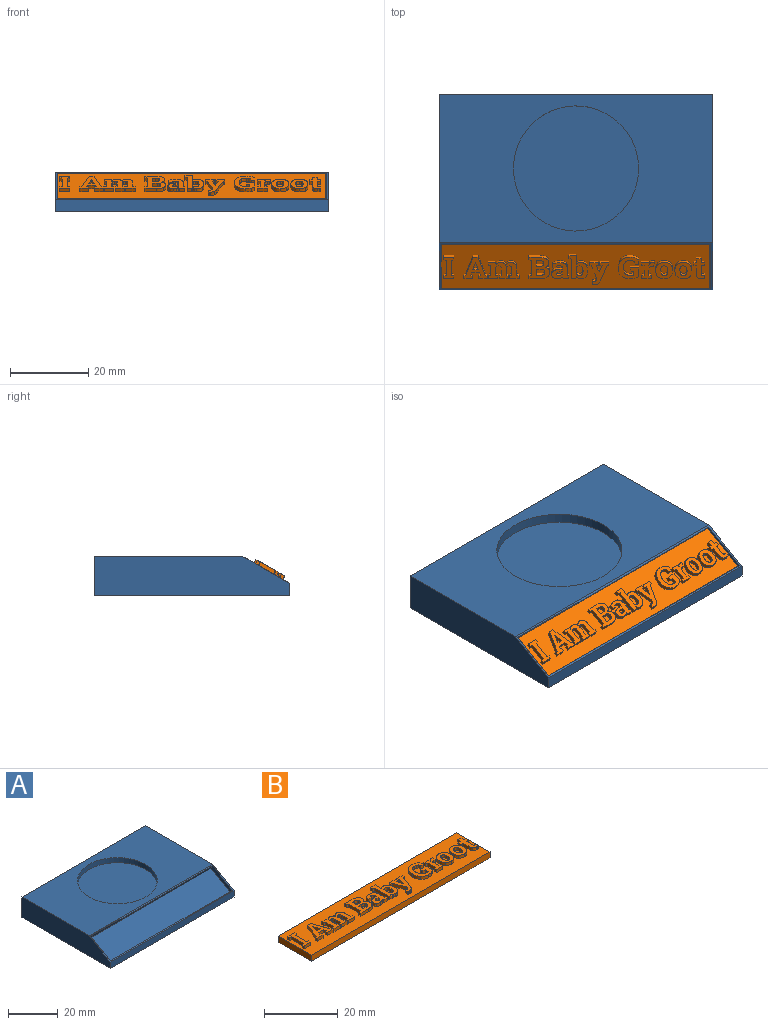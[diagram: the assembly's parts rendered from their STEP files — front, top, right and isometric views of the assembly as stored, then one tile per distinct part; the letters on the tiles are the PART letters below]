
ASSEMBLY  parts=2 mates=1
PART A: 14 faces, bbox 70x50x10 mm
  f0: plane 70x10mm, normal (0,1,0), area 700mm2, adj f1,f3,f4,f5
  f1: plane 50x10mm, normal (-1,0,0), area 458.4mm2, adj f0,f2,f4,f5,f6
  f2: plane 70x3.07mm, normal (0,-1,0), area 215mm2, adj f1,f3,f5,f6
  f3: plane 50x10mm, normal (1,0,0), area 458.4mm2, adj f0,f2,f4,f5,f6
  f4: plane 70x38mm, normal (0,0,1), area 1855.8mm2, adj f0,f1,f3,f6,f7
  f5: plane 70x50mm, normal (0,0,-1), area 3500mm2, adj f0,f1,f2,f3
  f6: plane 70x12mm, normal (0,-0.5,0.87), area 82.9mm2, adj f1,f2,f3,f4,f9,f10,f11,f12
  f7: cylinder r=16mm len=32mm, axis (0,0,1), area 251.3mm2, adj f4,f8
  f8: plane 32x32mm, normal (0,0,1), area 804.2mm2, adj f7
  f9: plane 12.13x8.16mm, normal (1,0,0), area 25.7mm2, adj f6,f10,f12,f13
  f10: plane 69x1.73mm, normal (0,0.87,0.5), area 138mm2, adj f6,f9,f11,f13
  f11: plane 12.13x8.16mm, normal (-1,0,0), area 25.7mm2, adj f6,f10,f12,f13
  f12: plane 69x1.73mm, normal (0,-0.87,-0.5), area 138mm2, adj f6,f9,f11,f13
  f13: plane 69x11.13mm, normal (0,-0.5,0.87), area 887.1mm2, adj f9,f10,f11,f12
PART B: 321 faces, bbox 68.5x12.7x3 mm
  f0: plane 68.5x12.7mm, normal (0,0,1), area 673mm2, adj f1,f2,f3,f4,f6,f7,f8,f9
  f1: plane 68.5x2mm, normal (0,1,0), area 137mm2, adj f0,f2,f4,f5
  f2: plane 12.7x2mm, normal (-1,0,0), area 25.4mm2, adj f0,f1,f3,f5
  f3: plane 68.5x2mm, normal (0,-1,0), area 137mm2, adj f0,f2,f4,f5
  f4: plane 12.7x2mm, normal (1,0,0), area 25.4mm2, adj f0,f1,f3,f5
  f5: plane 68.5x12.7mm, normal (0,0,-1), area 870mm2, adj f1,f2,f3,f4
  f6: plane 1x0.67mm, normal (-0.19,-0.98,0), area 0.7mm2, adj f0,f7,f17,f18
  f7: plane 4.46x1mm, normal (-1,0,0), area 4.5mm2, adj f0,f6,f8,f18
  f8: plane 1x0.67mm, normal (-0.19,0.98,0), area 0.7mm2, adj f0,f7,f9,f18
  f9: plane 1x0.75mm, normal (-1,0,0), area 0.7mm2, adj f0,f8,f10,f18
  f10: plane 2.57x1mm, normal (0,-1,0), area 2.6mm2, adj f0,f9,f11,f18
  f11: plane 1x0.75mm, normal (1,0,0), area 0.7mm2, adj f0,f10,f12,f18
  f12: plane 1x0.67mm, normal (0.19,0.98,0), area 0.7mm2, adj f0,f11,f13,f18
  f13: plane 4.46x1mm, normal (1,0,0), area 4.5mm2, adj f0,f12,f14,f18
  f14: plane 1x0.67mm, normal (0.19,-0.98,0), area 0.7mm2, adj f0,f13,f15,f18
  f15: plane 1x0.75mm, normal (1,0,0), area 0.8mm2, adj f0,f14,f16,f18
  f16: plane 2.57x1mm, normal (0,1,0), area 2.6mm2, adj f0,f15,f17,f18
  f17: plane 1x0.75mm, normal (-1,0,0), area 0.8mm2, adj f0,f6,f16,f18
  f18: plane 6.21x2.57mm, normal (0,0,1), area 9.9mm2, adj f6,f7,f8,f9,f10,f11,f12,f13
  f19: plane 1x0.75mm, normal (-1,0,0), area 0.7mm2, adj f0,f20,f38,f39
  f20: plane 2.12x1mm, normal (0,-1,0), area 2.1mm2, adj f0,f19,f21,f39
  f21: plane 1x0.75mm, normal (1,0,0), area 0.7mm2, adj f0,f20,f22,f39
  f22: plane 1x0.43mm, normal (0.18,0.98,0), area 0.4mm2, adj f0,f21,f23,f39
  f23: plane 1x0.85mm, normal (0.95,-0.3,0), area 0.9mm2, adj f0,f22,f24,f39
  f24: plane 2.01x1mm, normal (0,-1,0), area 2mm2, adj f0,f23,f25,f39
  f25: plane 1x0.85mm, normal (-0.95,-0.3,0), area 0.9mm2, adj f0,f24,f26,f39
  f26: plane 1x0.43mm, normal (-0.17,0.98,0), area 0.4mm2, adj f0,f25,f27,f39
  f27: plane 1x0.75mm, normal (-1,0,0), area 0.7mm2, adj f0,f26,f28,f39
  f28: plane 2.12x1mm, normal (0,-1,0), area 2.1mm2, adj f0,f27,f29,f39
  f29: plane 1x0.75mm, normal (1,0,0), area 0.7mm2, adj f0,f28,f30,f39
  f30: plane 1x0.44mm, normal (0.14,0.99,0), area 0.4mm2, adj f0,f29,f31,f39
  f31: plane 5.4x1.88mm, normal (0.94,0.33,0), area 5.7mm2, adj f0,f30,f32,f39
  f32: plane 1.28x1mm, normal (0,1,0), area 1.3mm2, adj f0,f31,f33,f39
  f33: plane 5.4x1.89mm, normal (-0.94,0.33,0), area 5.7mm2, adj f0,f32,f38,f39
  f34: plane 2.19x1mm, normal (0.95,-0.3,0), area 2.3mm2, adj f35,f37,f39,f40
  f35: plane 1x0.02mm, normal (0,-1,0), area 0mm2, adj f34,f36,f39,f40
  f36: plane 2.19x1mm, normal (-0.95,-0.3,0), area 2.3mm2, adj f35,f37,f39,f40
  f37: plane 1.43x1mm, normal (0,1,0), area 1.4mm2, adj f34,f36,f39,f40
  f38: plane 1x0.44mm, normal (-0.14,0.99,0), area 0.4mm2, adj f0,f19,f33,f39
  f39: plane 6.21x5.93mm, normal (0,0,1), area 16.9mm2, adj f19,f20,f21,f22,f23,f24,f25,f26
  f40: plane 2.19x1.43mm, normal (0,0,1), area 1.6mm2, adj f34,f35,f36,f37
  f41: plane 1x0.67mm, normal (-0.19,-0.98,0), area 0.7mm2, adj f0,f42,f83,f84
  f42: plane 2.86x1mm, normal (-1,0,0), area 2.9mm2, adj f0,f41,f43,f84
  f43: plane 1x0.6mm, normal (-0.21,0.98,0), area 0.6mm2, adj f0,f42,f44,f84
  f44: plane 1x0.75mm, normal (-1,0,0), area 0.7mm2, adj f0,f43,f45,f84
  f45: plane 2.38x1mm, normal (0,-1,0), area 2.4mm2, adj f0,f44,f46,f84
  f46: plane 1x0.75mm, normal (1,0,0), area 0.7mm2, adj f0,f45,f47,f84
  f47: plane 1x0.54mm, normal (0.23,0.97,0), area 0.6mm2, adj f0,f46,f48,f84
  f48: plane 2.49x1mm, normal (1,0,0), area 2.5mm2, adj f0,f47,f49,f84
  f49: extruded ~1x0.31mm, area 0.4mm2, adj f0,f48,f50,f84
  f50: extruded ~1x0.44mm, area 0.5mm2, adj f0,f49,f51,f84
  f51: extruded ~1x0.51mm, area 0.6mm2, adj f0,f50,f52,f84
  f52: extruded ~1x0.72mm, area 0.8mm2, adj f0,f51,f53,f84
  f53: plane 1.92x1mm, normal (-1,0,0), area 1.9mm2, adj f0,f52,f54,f84
  f54: plane 1x0.5mm, normal (-0.25,0.97,0), area 0.5mm2, adj f0,f53,f55,f84
  f55: plane 1x0.75mm, normal (-1,0,0), area 0.7mm2, adj f0,f54,f56,f84
  f56: plane 2.25x1mm, normal (0,-1,0), area 2.2mm2, adj f0,f55,f57,f84
  f57: plane 1x0.75mm, normal (1,0,0), area 0.7mm2, adj f0,f56,f58,f84
  f58: plane 1x0.5mm, normal (0.25,0.97,0), area 0.5mm2, adj f0,f57,f59,f84
  f59: plane 2.16x1mm, normal (1,0,0), area 2.2mm2, adj f0,f58,f60,f84
  f60: extruded ~1x0.12mm, area 0.1mm2, adj f0,f59,f61,f84
  f61: extruded ~1x0.14mm, area 0.1mm2, adj f0,f60,f62,f84
  f62: extruded ~1x0.33mm, area 0.5mm2, adj f0,f61,f63,f84
  f63: extruded ~1x0.46mm, area 0.5mm2, adj f0,f62,f64,f84
  f64: extruded ~1x0.51mm, area 0.6mm2, adj f0,f63,f65,f84
  f65: extruded ~1x0.73mm, area 0.8mm2, adj f0,f64,f66,f84
  f66: plane 1.92x1mm, normal (-1,0,0), area 1.9mm2, adj f0,f65,f67,f84
  f67: plane 1x0.54mm, normal (-0.23,0.97,0), area 0.6mm2, adj f0,f66,f68,f84
  f68: plane 1x0.75mm, normal (-1,0,0), area 0.7mm2, adj f0,f67,f69,f84
  f69: plane 2.39x1mm, normal (0,-1,0), area 2.4mm2, adj f0,f68,f70,f84
  f70: plane 1x0.75mm, normal (1,0,0), area 0.7mm2, adj f0,f69,f71,f84
  f71: plane 1x0.6mm, normal (0.21,0.98,0), area 0.6mm2, adj f0,f70,f72,f84
  f72: plane 1.92x1mm, normal (1,0,0), area 1.9mm2, adj f0,f71,f73,f84
  f73: extruded ~1.44x1mm, area 1.5mm2, adj f0,f72,f74,f84
  f74: extruded ~1.08x1mm, area 1.2mm2, adj f0,f73,f75,f84
  f75: extruded ~1x0.8mm, area 0.8mm2, adj f0,f74,f76,f84
  f76: extruded ~1x0.58mm, area 0.8mm2, adj f0,f75,f77,f84
  f77: extruded ~1x0.59mm, area 0.8mm2, adj f0,f76,f78,f84
  f78: extruded ~1x0.76mm, area 0.8mm2, adj f0,f77,f79,f84
  f79: extruded ~1x0.77mm, area 0.8mm2, adj f0,f78,f80,f84
  f80: extruded ~1x0.56mm, area 0.8mm2, adj f0,f79,f81,f84
  f81: plane 1x0.61mm, normal (1,0.08,0), area 0.6mm2, adj f0,f80,f82,f84
  f82: plane 1.82x1mm, normal (0,1,0), area 1.8mm2, adj f0,f81,f83,f84
  f83: plane 1x0.75mm, normal (-1,0,0), area 0.8mm2, adj f0,f41,f82,f84
  f84: plane 7.87x4.7mm, normal (0,0,1), area 22.5mm2, adj f41,f42,f43,f44,f45,f46,f47,f48
  f85: plane 2.76x1mm, normal (0,1,0), area 2.8mm2, adj f0,f86,f113,f114
  f86: plane 1x0.75mm, normal (-1,0,0), area 0.8mm2, adj f0,f85,f87,f114
  f87: plane 1x0.66mm, normal (-0.19,-0.98,0), area 0.7mm2, adj f0,f86,f88,f114
  f88: plane 4.46x1mm, normal (-1,0,0), area 4.5mm2, adj f0,f87,f89,f114
  f89: plane 1x0.66mm, normal (-0.19,0.98,0), area 0.7mm2, adj f0,f88,f90,f114
  f90: plane 1x0.75mm, normal (-1,0,0), area 0.7mm2, adj f0,f89,f91,f114
  f91: plane 3.06x1mm, normal (0,-1,0), area 3.1mm2, adj f0,f90,f92,f114
  f92: extruded ~1.67x1mm, area 1.8mm2, adj f0,f91,f93,f114
  f93: extruded ~1.35x1mm, area 1.5mm2, adj f0,f92,f94,f114
  f94: extruded ~1x0.91mm, area 1mm2, adj f0,f93,f95,f114
  f95: extruded ~1x0.84mm, area 1mm2, adj f0,f94,f96,f114
  f96: extruded ~1x0.66mm, area 0.9mm2, adj f0,f95,f97,f114
  f97: extruded ~1x0.77mm, area 0.8mm2, adj f0,f96,f98,f114
  f98: extruded ~1.28x1mm, area 1.5mm2, adj f0,f97,f113,f114
  f99: plane 1.24x1mm, normal (0,-1,0), area 1.2mm2, adj f100,f111,f114,f116
  f100: extruded ~1x0.7mm, area 0.8mm2, adj f99,f101,f114,f116
  f101: extruded ~1x0.7mm, area 0.7mm2, adj f100,f102,f114,f116
  f102: extruded ~1x0.64mm, area 0.7mm2, adj f101,f103,f114,f116
  f103: extruded ~1x0.75mm, area 0.8mm2, adj f102,f104,f114,f116
  f104: plane 1.15x1mm, normal (0,1,0), area 1.1mm2, adj f103,f111,f114,f116
  f105: plane 1.64x1mm, normal (1,0,0), area 1.6mm2, adj f106,f112,f114,f115
  f106: plane 1x0.85mm, normal (0,-1,0), area 0.9mm2, adj f105,f107,f114,f115
  f107: extruded ~1x0.81mm, area 0.8mm2, adj f106,f108,f114,f115
  f108: extruded ~1x0.64mm, area 0.7mm2, adj f107,f109,f114,f115
  f109: extruded ~1x0.6mm, area 0.7mm2, adj f108,f110,f114,f115
  f110: extruded ~1x0.77mm, area 0.8mm2, adj f109,f112,f114,f115
  f111: plane 1.79x1mm, normal (1,0,0), area 1.8mm2, adj f99,f104,f114,f116
  f112: plane 1x0.9mm, normal (0,1,0), area 0.9mm2, adj f105,f110,f114,f115
  f113: extruded ~1.71x1mm, area 1.8mm2, adj f0,f85,f98,f114
  f114: plane 6.21x5.31mm, normal (0,0,1), area 20.7mm2, adj f85,f86,f87,f88,f89,f90,f91,f92
  f115: plane 1.93x1.64mm, normal (0,0,1), area 2.9mm2, adj f105,f106,f107,f108,f109,f110,f112
  f116: plane 2.16x1.79mm, normal (0,0,1), area 3.6mm2, adj f99,f100,f101,f102,f103,f104,f111
  f117: plane 1.44x1mm, normal (0,-1,0), area 1.4mm2, adj f0,f118,f151,f152
  f118: plane 1x0.75mm, normal (1,0,0), area 0.7mm2, adj f0,f117,f119,f152
  f119: plane 1x0.38mm, normal (0.13,0.99,0), area 0.4mm2, adj f0,f118,f120,f152
  f120: extruded ~1x0.18mm, area 0.2mm2, adj f0,f119,f121,f152
  f121: extruded ~1x0.2mm, area 0.2mm2, adj f0,f120,f122,f152
  f122: plane 1.91x1mm, normal (1,0,0), area 1.9mm2, adj f0,f121,f123,f152
  f123: extruded ~1.2x1mm, area 1.4mm2, adj f0,f122,f124,f152
  f124: extruded ~1.39x1mm, area 1.5mm2, adj f0,f123,f125,f152
  f125: extruded ~1x0.96mm, area 1mm2, adj f0,f124,f126,f152
  f126: extruded ~1x0.78mm, area 0.9mm2, adj f0,f125,f127,f152
  f127: plane 1.02x1mm, normal (-1,0,0), area 1mm2, adj f0,f126,f128,f152
  f128: plane 1x0.94mm, normal (0,-1,0), area 0.9mm2, adj f0,f127,f129,f152
  f129: plane 1x0.49mm, normal (0.99,-0.16,0), area 0.5mm2, adj f0,f128,f130,f152
  f130: extruded ~1x0.27mm, area 0.3mm2, adj f0,f129,f131,f152
  f131: extruded ~1x0.38mm, area 0.4mm2, adj f0,f130,f132,f152
  f132: extruded ~1x0.57mm, area 0.6mm2, adj f0,f131,f133,f152
  f133: extruded ~1x0.52mm, area 0.6mm2, adj f0,f132,f134,f152
  f134: plane 1x0.45mm, normal (-1,0,0), area 0.5mm2, adj f0,f133,f135,f152
  f135: plane 1x0.64mm, normal (0,1,0), area 0.6mm2, adj f0,f134,f136,f152
  f136: extruded ~1.53x1mm, area 1.6mm2, adj f0,f135,f137,f152
  f137: extruded ~1x1mm, area 1.2mm2, adj f0,f136,f138,f152
  f138: extruded ~1.01x1mm, area 1.1mm2, adj f0,f137,f139,f152
  f139: extruded ~1.08x1mm, area 1.2mm2, adj f0,f138,f140,f152
  f140: extruded ~1x0.73mm, area 0.8mm2, adj f0,f139,f141,f152
  f141: extruded ~1x0.54mm, area 0.7mm2, adj f0,f140,f142,f152
  f142: extruded ~1x0.25mm, area 0.3mm2, adj f0,f141,f151,f152
  f143: extruded ~1x0.42mm, area 0.4mm2, adj f144,f150,f152,f153
  f144: extruded ~1x0.37mm, area 0.4mm2, adj f143,f145,f152,f153
  f145: extruded ~1x0.45mm, area 0.5mm2, adj f144,f146,f152,f153
  f146: extruded ~1x0.6mm, area 0.6mm2, adj f145,f147,f152,f153
  f147: plane 1x0.64mm, normal (0,-1,0), area 0.6mm2, adj f146,f148,f152,f153
  f148: plane 1x0.7mm, normal (-1,0,0), area 0.7mm2, adj f147,f149,f152,f153
  f149: extruded ~1x0.36mm, area 0.5mm2, adj f148,f150,f152,f153
  f150: extruded ~1x0.51mm, area 0.5mm2, adj f143,f149,f152,f153
  f151: extruded ~1x0.24mm, area 0.3mm2, adj f0,f117,f142,f152
  f152: plane 4.79x4.33mm, normal (0,0,1), area 13.1mm2, adj f117,f118,f119,f120,f121,f122,f123,f124
  f153: plane 1.44x1.13mm, normal (0,0,1), area 1.4mm2, adj f143,f144,f145,f146,f147,f148,f149,f150
  f154: plane 1x0.09mm, normal (1,0,0), area 0.1mm2, adj f0,f155,f179,f180
  f155: extruded ~1.77x1mm, area 1.9mm2, adj f0,f154,f156,f180
  f156: extruded ~1.34x1mm, area 1.6mm2, adj f0,f155,f157,f180
  f157: extruded ~1x0.64mm, area 0.7mm2, adj f0,f156,f158,f180
  f158: extruded ~1x0.48mm, area 0.6mm2, adj f0,f157,f159,f180
  f159: plane 2.53x1mm, normal (1,0,0), area 2.5mm2, adj f0,f158,f160,f180
  f160: plane 1.9x1mm, normal (0,1,0), area 1.9mm2, adj f0,f159,f161,f180
  f161: plane 1x0.75mm, normal (-1,0,0), area 0.8mm2, adj f0,f160,f162,f180
  f162: plane 1x0.66mm, normal (-0.19,-0.98,0), area 0.7mm2, adj f0,f161,f163,f180
  f163: plane 5.78x1mm, normal (-1,0,0), area 5.8mm2, adj f0,f162,f164,f180
  f164: plane 1.07x1mm, normal (0,-1,0), area 1.1mm2, adj f0,f163,f165,f180
  f165: plane 1x0.57mm, normal (0.99,-0.16,0), area 0.6mm2, adj f0,f164,f166,f180
  f166: extruded ~1x0.5mm, area 0.7mm2, adj f0,f165,f167,f180
  f167: extruded ~1x0.7mm, area 0.7mm2, adj f0,f166,f168,f180
  f168: extruded ~1.33x1mm, area 1.5mm2, adj f0,f167,f179,f180
  f169: plane 1x0.09mm, normal (-1,0,0), area 0.1mm2, adj f170,f178,f180,f181
  f170: extruded ~1x0.96mm, area 1mm2, adj f169,f171,f180,f181
  f171: extruded ~1x0.67mm, area 0.8mm2, adj f170,f172,f180,f181
  f172: extruded ~1x0.5mm, area 0.5mm2, adj f171,f173,f180,f181
  f173: extruded ~1x0.33mm, area 0.5mm2, adj f172,f174,f180,f181
  f174: plane 1.95x1mm, normal (1,0,0), area 1.9mm2, adj f173,f175,f180,f181
  f175: extruded ~1x0.35mm, area 0.5mm2, adj f174,f176,f180,f181
  f176: extruded ~1x0.49mm, area 0.5mm2, adj f175,f177,f180,f181
  f177: extruded ~1x0.68mm, area 0.8mm2, adj f176,f178,f180,f181
  f178: extruded ~1.07x1mm, area 1.1mm2, adj f169,f177,f180,f181
  f179: extruded ~1.65x1mm, area 1.7mm2, adj f0,f154,f168,f180
  f180: plane 6.75x4.83mm, normal (0,0,1), area 16.6mm2, adj f154,f155,f156,f157,f158,f159,f160,f161
  f181: plane 2.85x1.68mm, normal (0,0,1), area 4.2mm2, adj f169,f170,f171,f172,f173,f174,f175,f176
  f182: plane 1x0.75mm, normal (1,0,0), area 0.8mm2, adj f0,f183,f207,f208
  f183: plane 2.26x1mm, normal (0,1,0), area 2.3mm2, adj f0,f182,f184,f208
  f184: plane 1x0.75mm, normal (-1,0,0), area 0.8mm2, adj f0,f183,f185,f208
  f185: plane 1x0.52mm, normal (-0.16,-0.99,0), area 0.5mm2, adj f0,f184,f186,f208
  f186: plane 2.18x1mm, normal (-0.95,0.32,0), area 2.3mm2, adj f0,f185,f187,f208
  f187: plane 1x0.03mm, normal (0.16,0.99,0), area 0mm2, adj f0,f186,f188,f208
  f188: plane 1x0.33mm, normal (0.98,0.19,0), area 0.3mm2, adj f0,f187,f189,f208
  f189: plane 1.84x1mm, normal (0.95,0.32,0), area 1.9mm2, adj f0,f188,f190,f208
  f190: plane 1x0.52mm, normal (0.16,-0.99,0), area 0.5mm2, adj f0,f189,f191,f208
  f191: plane 1x0.75mm, normal (1,0,0), area 0.8mm2, adj f0,f190,f192,f208
  f192: plane 2.26x1mm, normal (0,1,0), area 2.3mm2, adj f0,f191,f193,f208
  f193: plane 1x0.75mm, normal (-1,0,0), area 0.8mm2, adj f0,f192,f194,f208
  f194: plane 1x0.43mm, normal (-0.16,-0.99,0), area 0.4mm2, adj f0,f193,f195,f208
  f195: plane 3.8x1.46mm, normal (-0.93,-0.36,0), area 4.1mm2, adj f0,f194,f196,f208
  f196: plane 1x0.35mm, normal (-0.93,0.37,0), area 0.4mm2, adj f0,f195,f197,f208
  f197: extruded ~1x0.38mm, area 0.5mm2, adj f0,f196,f198,f208
  f198: extruded ~1x0.48mm, area 0.5mm2, adj f0,f197,f199,f208
  f199: extruded ~1x0.11mm, area 0.1mm2, adj f0,f198,f200,f208
  f200: extruded ~1x0.12mm, area 0.1mm2, adj f0,f199,f201,f208
  f201: plane 1x0.91mm, normal (-0.99,0.16,0), area 0.9mm2, adj f0,f200,f202,f208
  f202: extruded ~1x0.33mm, area 0.3mm2, adj f0,f201,f203,f208
  f203: extruded ~1x0.3mm, area 0.3mm2, adj f0,f202,f204,f208
  f204: extruded ~1.01x1mm, area 1.1mm2, adj f0,f203,f205,f208
  f205: extruded ~1x0.84mm, area 1mm2, adj f0,f204,f206,f208
  f206: plane 4.49x1.7mm, normal (0.94,-0.35,0), area 4.8mm2, adj f0,f205,f207,f208
  f207: plane 1x0.43mm, normal (0.15,-0.99,0), area 0.4mm2, adj f0,f182,f206,f208
  f208: plane 6.48x4.94mm, normal (0,0,1), area 14.7mm2, adj f182,f183,f184,f185,f186,f187,f188,f189
  f209: plane 2.39x1mm, normal (1,0,0), area 2.4mm2, adj f0,f210,f234,f235
  f210: plane 2.14x1mm, normal (0,1,0), area 2.1mm2, adj f0,f209,f211,f235
  f211: plane 1x0.87mm, normal (-1,0,0), area 0.9mm2, adj f0,f210,f212,f235
  f212: plane 1x0.89mm, normal (-0.08,-1,0), area 0.9mm2, adj f0,f211,f213,f235
  f213: plane 1.05x1mm, normal (-1,0,0), area 1.1mm2, adj f0,f212,f214,f235
  f214: extruded ~1x0.36mm, area 0.4mm2, adj f0,f213,f215,f235
  f215: extruded ~1x0.61mm, area 0.6mm2, adj f0,f214,f216,f235
  f216: extruded ~1.28x1mm, area 1.5mm2, adj f0,f215,f217,f235
  f217: extruded ~1.51x1mm, area 1.6mm2, adj f0,f216,f218,f235
  f218: plane 1x0.22mm, normal (1,0,0), area 0.2mm2, adj f0,f217,f219,f235
  f219: extruded ~1.57x1mm, area 1.7mm2, adj f0,f218,f220,f235
  f220: extruded ~1.27x1mm, area 1.5mm2, adj f0,f219,f221,f235
  f221: extruded ~1x0.64mm, area 0.7mm2, adj f0,f220,f222,f235
  f222: extruded ~1x0.45mm, area 0.5mm2, adj f0,f221,f223,f235
  f223: plane 1x0.83mm, normal (-0.98,-0.21,0), area 0.8mm2, adj f0,f222,f224,f235
  f224: plane 1x0.92mm, normal (0,-1,0), area 0.9mm2, adj f0,f223,f225,f235
  f225: plane 1.25x1mm, normal (1,0,0), area 1.2mm2, adj f0,f224,f226,f235
  f226: extruded ~1x1mm, area 1.2mm2, adj f0,f225,f227,f235
  f227: extruded ~1.33x1mm, area 1.4mm2, adj f0,f226,f228,f235
  f228: extruded ~2.03x1mm, area 2.3mm2, adj f0,f227,f229,f235
  f229: extruded ~2.27x1mm, area 2.5mm2, adj f0,f228,f230,f235
  f230: plane 1x0.21mm, normal (-1,0,0), area 0.2mm2, adj f0,f229,f231,f235
  f231: extruded ~2.19x1mm, area 2.4mm2, adj f0,f230,f232,f235
  f232: extruded ~2.05x1mm, area 2.3mm2, adj f0,f231,f233,f235
  f233: extruded ~1.47x1mm, area 1.5mm2, adj f0,f232,f234,f235
  f234: extruded ~1x0.88mm, area 1mm2, adj f0,f209,f233,f235
  f235: plane 6.39x5.19mm, normal (0,0,1), area 17.2mm2, adj f209,f210,f211,f212,f213,f214,f215,f216
  f236: plane 1x0.75mm, normal (-1,0,0), area 0.7mm2, adj f0,f237,f254,f255
  f237: plane 2.44x1mm, normal (0,-1,0), area 2.4mm2, adj f0,f236,f238,f255
  f238: plane 1x0.75mm, normal (1,0,0), area 0.7mm2, adj f0,f237,f239,f255
  f239: plane 1x0.6mm, normal (0.21,0.98,0), area 0.6mm2, adj f0,f238,f240,f255
  f240: plane 2.24x1mm, normal (1,0,0), area 2.2mm2, adj f0,f239,f241,f255
  f241: extruded ~1x0.3mm, area 0.4mm2, adj f0,f240,f242,f255
  f242: extruded ~1x0.45mm, area 0.5mm2, adj f0,f241,f243,f255
  f243: plane 1x0.51mm, normal (-0.02,-1,0), area 0.5mm2, adj f0,f242,f244,f255
  f244: plane 1.13x1mm, normal (0.99,-0.12,0), area 1.1mm2, adj f0,f243,f245,f255
  f245: extruded ~1x0.18mm, area 0.2mm2, adj f0,f244,f246,f255
  f246: extruded ~1x0.21mm, area 0.2mm2, adj f0,f245,f247,f255
  f247: extruded ~1x0.59mm, area 0.6mm2, adj f0,f246,f248,f255
  f248: extruded ~1x0.56mm, area 0.7mm2, adj f0,f247,f249,f255
  f249: plane 1x0.67mm, normal (1,0.08,0), area 0.7mm2, adj f0,f248,f250,f255
  f250: plane 1.82x1mm, normal (0,1,0), area 1.8mm2, adj f0,f249,f251,f255
  f251: plane 1x0.75mm, normal (-1,0,0), area 0.8mm2, adj f0,f250,f252,f255
  f252: plane 1x0.66mm, normal (-0.19,-0.98,0), area 0.7mm2, adj f0,f251,f253,f255
  f253: plane 2.86x1mm, normal (-1,0,0), area 2.9mm2, adj f0,f252,f254,f255
  f254: plane 1x0.6mm, normal (-0.21,0.98,0), area 0.6mm2, adj f0,f236,f253,f255
  f255: plane 4.7x3.28mm, normal (0,0,1), area 8.6mm2, adj f236,f237,f238,f239,f240,f241,f242,f243
  f256: plane 1x0.09mm, normal (-1,0,0), area 0.1mm2, adj f0,f257,f275,f276
  f257: extruded ~1.7x1mm, area 1.8mm2, adj f0,f256,f258,f276
  f258: extruded ~1.61x1mm, area 1.8mm2, adj f0,f257,f259,f276
  f259: extruded ~1.59x1mm, area 1.8mm2, adj f0,f258,f260,f276
  f260: extruded ~1.7x1mm, area 1.8mm2, adj f0,f259,f261,f276
  f261: plane 1x0.09mm, normal (1,0,0), area 0.1mm2, adj f0,f260,f262,f276
  f262: extruded ~1.69x1mm, area 1.8mm2, adj f0,f261,f263,f276
  f263: extruded ~1.6x1mm, area 1.8mm2, adj f0,f262,f264,f276
  f264: extruded ~1.6x1mm, area 1.8mm2, adj f0,f263,f275,f276
  f265: plane 1x0.09mm, normal (1,0,0), area 0.1mm2, adj f266,f274,f276,f277
  f266: extruded ~1x1mm, area 1mm2, adj f265,f267,f276,f277
  f267: extruded ~1x0.71mm, area 0.9mm2, adj f266,f268,f276,f277
  f268: extruded ~1x0.71mm, area 0.9mm2, adj f267,f269,f276,f277
  f269: extruded ~1x1mm, area 1mm2, adj f268,f270,f276,f277
  f270: plane 1x0.09mm, normal (-1,0,0), area 0.1mm2, adj f269,f271,f276,f277
  f271: extruded ~1.01x1mm, area 1mm2, adj f270,f272,f276,f277
  f272: extruded ~1x0.71mm, area 0.8mm2, adj f271,f273,f276,f277
  f273: extruded ~1x0.72mm, area 0.9mm2, adj f272,f274,f276,f277
  f274: extruded ~1.01x1mm, area 1mm2, adj f265,f273,f276,f277
  f275: extruded ~1.69x1mm, area 1.8mm2, adj f0,f256,f264,f276
  f276: plane 4.79x4.36mm, normal (0,0,1), area 12.5mm2, adj f256,f257,f258,f259,f260,f261,f262,f263
  f277: plane 2.88x1.87mm, normal (0,0,1), area 4.5mm2, adj f265,f266,f267,f268,f269,f270,f271,f272
  f278: plane 1x0.09mm, normal (-1,0,0), area 0.1mm2, adj f0,f279,f297,f298
  f279: extruded ~1.7x1mm, area 1.8mm2, adj f0,f278,f280,f298
  f280: extruded ~1.61x1mm, area 1.8mm2, adj f0,f279,f281,f298
  f281: extruded ~1.59x1mm, area 1.8mm2, adj f0,f280,f282,f298
  f282: extruded ~1.7x1mm, area 1.8mm2, adj f0,f281,f283,f298
  f283: plane 1x0.09mm, normal (1,0,0), area 0.1mm2, adj f0,f282,f284,f298
  f284: extruded ~1.69x1mm, area 1.8mm2, adj f0,f283,f285,f298
  f285: extruded ~1.6x1mm, area 1.8mm2, adj f0,f284,f286,f298
  f286: extruded ~1.6x1mm, area 1.8mm2, adj f0,f285,f297,f298
  f287: plane 1x0.09mm, normal (1,0,0), area 0.1mm2, adj f288,f296,f298,f299
  f288: extruded ~1x1mm, area 1mm2, adj f287,f289,f298,f299
  f289: extruded ~1x0.71mm, area 0.9mm2, adj f288,f290,f298,f299
  f290: extruded ~1x0.71mm, area 0.9mm2, adj f289,f291,f298,f299
  f291: extruded ~1x1mm, area 1mm2, adj f290,f292,f298,f299
  f292: plane 1x0.09mm, normal (-1,0,0), area 0.1mm2, adj f291,f293,f298,f299
  f293: extruded ~1.01x1mm, area 1mm2, adj f292,f294,f298,f299
  f294: extruded ~1x0.71mm, area 0.8mm2, adj f293,f295,f298,f299
  f295: extruded ~1x0.72mm, area 0.9mm2, adj f294,f296,f298,f299
  f296: extruded ~1.01x1mm, area 1mm2, adj f287,f295,f298,f299
  f297: extruded ~1.69x1mm, area 1.8mm2, adj f0,f278,f286,f298
  f298: plane 4.79x4.36mm, normal (0,0,1), area 12.5mm2, adj f278,f279,f280,f281,f282,f283,f284,f285
  f299: plane 2.88x1.87mm, normal (0,0,1), area 4.5mm2, adj f287,f288,f289,f290,f291,f292,f293,f294
  f300: plane 1.24x1mm, normal (0,1,0), area 1.2mm2, adj f0,f301,f319,f320
  f301: plane 1.13x1mm, normal (-1,0,0), area 1.1mm2, adj f0,f300,f302,f320
  f302: plane 1x0.68mm, normal (0,1,0), area 0.7mm2, adj f0,f301,f303,f320
  f303: plane 1x0.87mm, normal (-1,0,0), area 0.9mm2, adj f0,f302,f304,f320
  f304: plane 1x0.68mm, normal (0,-1,0), area 0.7mm2, adj f0,f303,f305,f320
  f305: plane 2.36x1mm, normal (-1,0,0), area 2.4mm2, adj f0,f304,f306,f320
  f306: extruded ~1.12x1mm, area 1.2mm2, adj f0,f305,f307,f320
  f307: extruded ~1x0.99mm, area 1.1mm2, adj f0,f306,f308,f320
  f308: extruded ~1x0.44mm, area 0.4mm2, adj f0,f307,f309,f320
  f309: extruded ~1x0.41mm, area 0.4mm2, adj f0,f308,f310,f320
  f310: plane 1x0.9mm, normal (0.99,0.12,0), area 0.9mm2, adj f0,f309,f311,f320
  f311: extruded ~1x0.22mm, area 0.2mm2, adj f0,f310,f312,f320
  f312: extruded ~1x0.22mm, area 0.2mm2, adj f0,f311,f313,f320
  f313: extruded ~1x0.3mm, area 0.3mm2, adj f0,f312,f314,f320
  f314: extruded ~1x0.38mm, area 0.4mm2, adj f0,f313,f315,f320
  f315: plane 2.35x1mm, normal (1,0,0), area 2.4mm2, adj f0,f314,f316,f320
  f316: plane 1x0.81mm, normal (0,-1,0), area 0.8mm2, adj f0,f315,f317,f320
  f317: plane 1x0.87mm, normal (1,0,0), area 0.9mm2, adj f0,f316,f318,f320
  f318: plane 1x0.81mm, normal (0,1,0), area 0.8mm2, adj f0,f317,f319,f320
  f319: plane 1.13x1mm, normal (1,0,0), area 1.1mm2, adj f0,f300,f318,f320
  f320: plane 5.84x2.88mm, normal (0,0,1), area 9.1mm2, adj f300,f301,f302,f303,f304,f305,f306,f307
PLACE A at identity
PLACE B rot(axis=(1,0,0),30deg) t=(2.82,-12.06,5.19)mm
MATE planar B.f5 <-> A.f13  axis (0,0.5,-0.87) through (4.89,-12.78,4.78)mm
